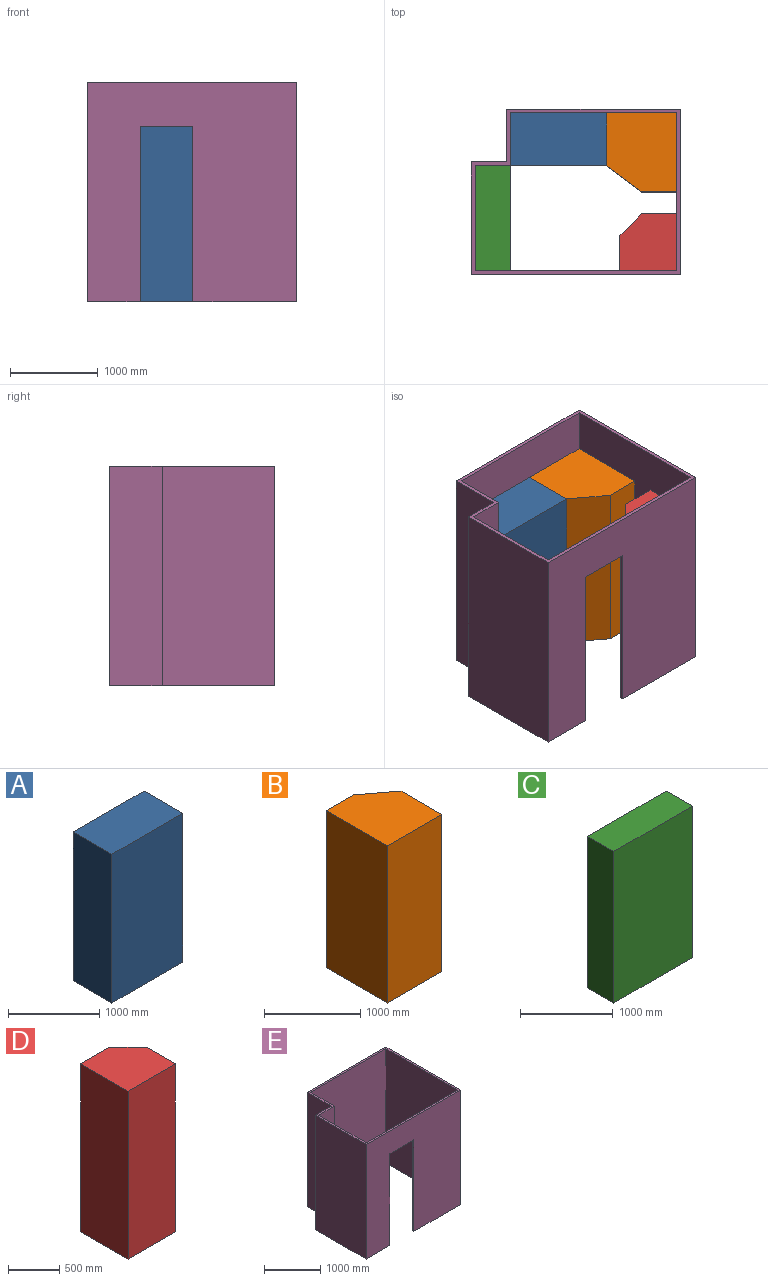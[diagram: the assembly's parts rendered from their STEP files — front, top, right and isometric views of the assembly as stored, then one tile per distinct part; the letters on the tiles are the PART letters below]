
ASSEMBLY  parts=5 mates=5
PART A: 6 faces, bbox 1100x600x2000 mm
  f0: plane 2000x600mm, normal (-1,0,0), area 1200000mm2, adj f1,f3,f4,f5
  f1: plane 2000x1100mm, normal (0,-1,0), area 2200000mm2, adj f0,f2,f4,f5
  f2: plane 2000x600mm, normal (1,0,0), area 1200000mm2, adj f1,f3,f4,f5
  f3: plane 2000x1100mm, normal (0,1,0), area 2200000mm2, adj f0,f2,f4,f5
  f4: plane 1100x600mm, normal (0,0,1), area 660000mm2, adj f0,f1,f2,f3
  f5: plane 1100x600mm, normal (0,0,-1), area 660000mm2, adj f0,f1,f2,f3
PART B: 7 faces, bbox 800x900x2000 mm
  f0: plane 2000x900mm, normal (-1,0,0), area 1800000mm2, adj f1,f4,f5,f6
  f1: plane 2000x800mm, normal (0,-1,0), area 1600000mm2, adj f0,f2,f5,f6
  f2: plane 2000x600mm, normal (1,0,0), area 1200000mm2, adj f1,f3,f5,f6
  f3: plane 2000x400mm, normal (0.6,0.8,0), area 1000000mm2, adj f2,f4,f5,f6
  f4: plane 2000x400mm, normal (0,1,0), area 800000mm2, adj f0,f3,f5,f6
  f5: plane 900x800mm, normal (0,0,1), area 660000mm2, adj f0,f1,f2,f3,f4
  f6: plane 900x800mm, normal (0,0,-1), area 660000mm2, adj f0,f1,f2,f3,f4
PART C: 6 faces, bbox 1200x400x2000 mm
  f0: plane 2000x400mm, normal (-1,0,0), area 800000mm2, adj f1,f3,f4,f5
  f1: plane 2000x1200mm, normal (0,-1,0), area 2400000mm2, adj f0,f2,f4,f5
  f2: plane 2000x400mm, normal (1,0,0), area 800000mm2, adj f1,f3,f4,f5
  f3: plane 2000x1200mm, normal (0,1,0), area 2400000mm2, adj f0,f2,f4,f5
  f4: plane 1200x400mm, normal (0,0,1), area 480000mm2, adj f0,f1,f2,f3
  f5: plane 1200x400mm, normal (0,0,-1), area 480000mm2, adj f0,f1,f2,f3
PART D: 7 faces, bbox 650x650x2000 mm
  f0: plane 2000x650mm, normal (-1,0,0), area 1300000mm2, adj f1,f4,f5,f6
  f1: plane 2000x650mm, normal (0,-1,0), area 1300000mm2, adj f0,f2,f5,f6
  f2: plane 2000x400mm, normal (1,0,0), area 800000mm2, adj f1,f3,f5,f6
  f3: plane 2000x250mm, normal (0.71,0.71,0), area 707106.8mm2, adj f2,f4,f5,f6
  f4: plane 2000x400mm, normal (0,1,0), area 800000mm2, adj f0,f3,f5,f6
  f5: plane 650x650mm, normal (0,0,1), area 391250mm2, adj f0,f1,f2,f3,f4
  f6: plane 650x650mm, normal (0,0,-1), area 391250mm2, adj f0,f1,f2,f3,f4
PART E: 17 faces, bbox 2380x1880x2500 mm
  f0: plane 2500x1980mm, normal (0,1,0), area 4950000mm2, adj f1,f11,f12,f13
  f1: plane 2500x600mm, normal (-1,0,0), area 1500000mm2, adj f0,f2,f12,f13
  f2: plane 2500x400mm, normal (0,1,0), area 1000000mm2, adj f1,f3,f12,f13
  f3: plane 2500x1280mm, normal (-1,0,0), area 3200000mm2, adj f2,f4,f12,f13
  f4: plane 2500x2380mm, normal (0,-1,0), area 4750000mm2, adj f3,f11,f12,f13,f14,f15,f16
  f5: plane 2500x2300mm, normal (0,1,0), area 4550000mm2, adj f6,f10,f12,f13,f14,f15,f16
  f6: plane 2500x1200mm, normal (1,0,0), area 3000000mm2, adj f5,f7,f12,f13
  f7: plane 2500x400mm, normal (0,-1,0), area 1000000mm2, adj f6,f8,f12,f13
  f8: plane 2500x600mm, normal (1,0,0), area 1500000mm2, adj f7,f9,f12,f13
  f9: plane 2500x1900mm, normal (0,-1,0), area 4750000mm2, adj f8,f10,f12,f13
  f10: plane 2500x1800mm, normal (-1,0,0), area 4500000mm2, adj f5,f9,f12,f13
  f11: plane 2500x1880mm, normal (1,0,0), area 4700000mm2, adj f0,f4,f12,f13
  f12: plane 2380x1880mm, normal (0,0,1), area 334400mm2, adj f0,f1,f2,f3,f4,f5,f6,f7
  f13: plane 2380x1880mm, normal (0,0,-1), area 310400mm2, adj f0,f1,f2,f3,f4,f5,f6,f7
  f14: plane 2000x40mm, normal (1,0,0), area 80000mm2, adj f4,f5,f13,f16
  f15: plane 2000x40mm, normal (-1,0,0), area 80000mm2, adj f4,f5,f13,f16
  f16: plane 600x40mm, normal (0,0,-1), area 24000mm2, adj f4,f5,f14,f15
PLACE A t=(250.6,1561.71,-223.98)mm
PLACE B rot(axis=(0,0,1),180deg) t=(2150.6,2161.71,-223.98)mm
PLACE C rot(axis=(0.71,0.71,0),180deg) t=(-149.4,361.71,1776.02)mm
PLACE D rot(axis=(0,0,1),90deg) t=(2150.6,361.71,-223.98)mm
PLACE E t=(-149.4,361.71,-223.98)mm fixed
MATE fastened D.f6 <-> E.f13  axis (0,0,-1) through (2150.6,361.71,-223.98)mm
MATE fastened C.f4 <-> E.f13  axis (0,0,-1) through (-149.4,361.71,-223.98)mm
MATE parallel E.f7 <-> C.f0  axis (0,-1,0) through (50.6,1561.71,1026.02)mm
MATE fastened A.f5 <-> E.f13  axis (0,0,1) through (250.6,2161.71,-223.98)mm
MATE fastened B.f6 <-> A.f5  axis (0,0,-1) through (1350.6,1561.71,-223.98)mm
